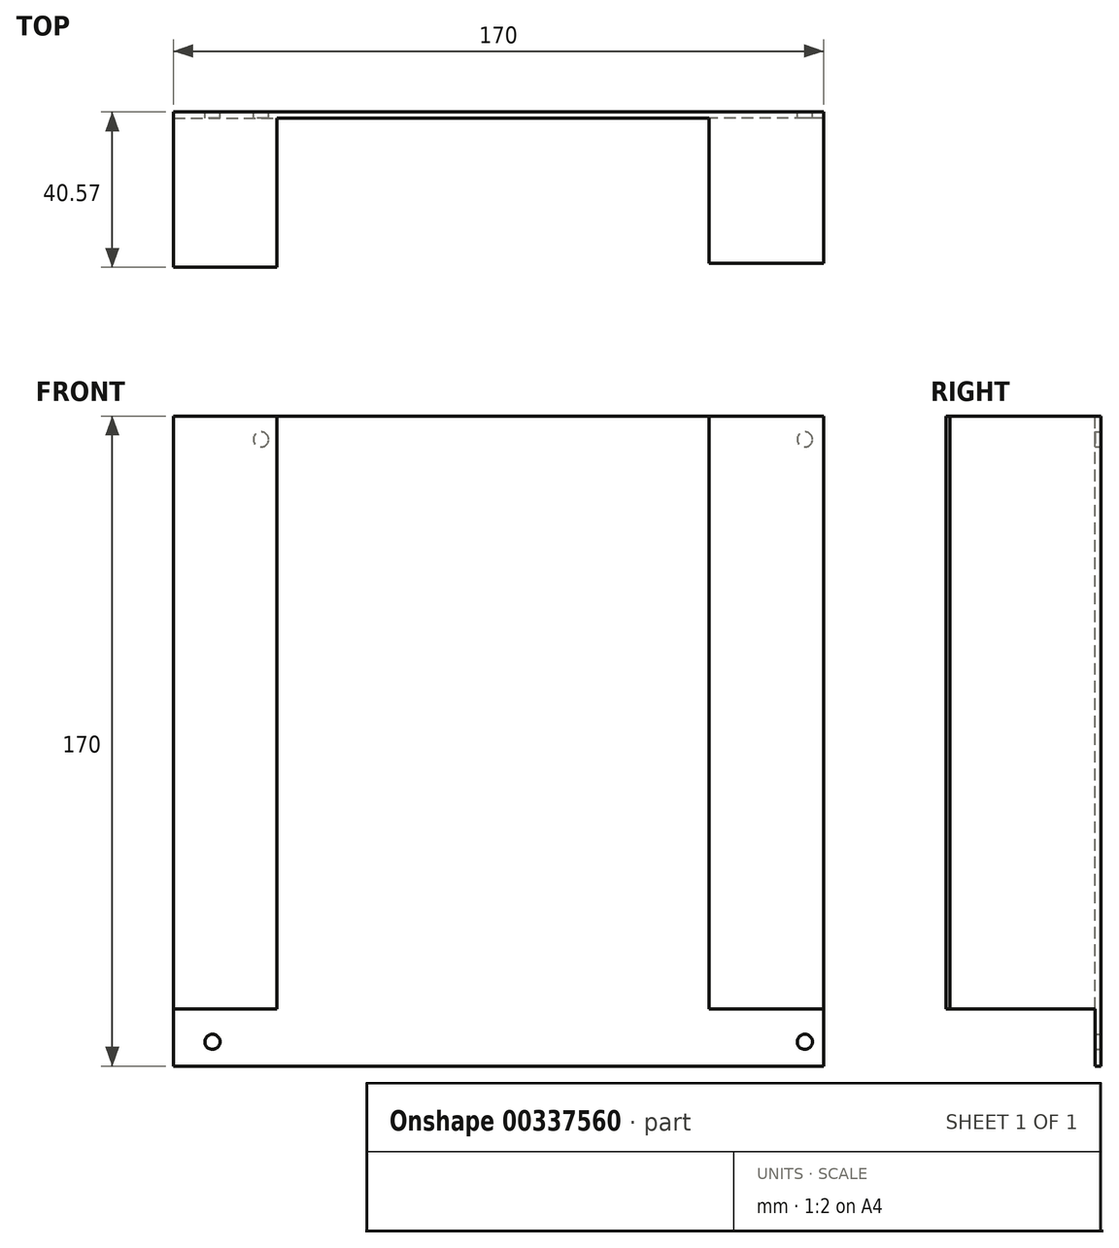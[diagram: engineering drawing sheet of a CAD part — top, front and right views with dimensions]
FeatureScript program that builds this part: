
annotation { "Feature Type Name" : "Feature", "Feature Type Description" : "" }
export const myFeature = defineFeature(function(context is Context, id is Id, definition is map)
    precondition{}
    {
        {
            var Q0;
            Q0=qCreatedBy(makeId("Front.planeOp"),FACE);
            var sketch = newSketch(context, id + "F0", { "sketchPlane" : qUnion([Q0])});
            skLineSegment(sketch, "E0.bottom", {"start": v(0, 0) * mm, "end": v(170, 0) * mm});
            skLineSegment(sketch, "E0.top", {"start": v(0, 170) * mm, "end": v(170, 170) * mm});
            skLineSegment(sketch, "E0.left", {"start": v(0, 0) * mm, "end": v(0, 170) * mm});
            skLineSegment(sketch, "E0.right", {"start": v(170, 0) * mm, "end": v(170, 170) * mm});
            skCircle(sketch, "E1", {"center": v(6.35, 4.88) * mm, "radius": 1.98 * mm});
            skCircle(sketch, "E2", {"center": v(6.35, 159.84) * mm, "radius": 1.98 * mm});
            skCircle(sketch, "E3", {"center": v(163.93, 147.14) * mm, "radius": 1.98 * mm});
            skCircle(sketch, "E4", {"center": v(163.93, 4.88) * mm, "radius": 1.98 * mm});
            skLineSegment(sketch, "E5", {"start": v(6.35, 159.84) * mm, "end": v(6.35, 4.88) * mm, "construction": true});
            skLineSegment(sketch, "E6", {"start": v(163.93, 4.88) * mm, "end": v(6.35, 4.88) * mm, "construction": true});
            skLineSegment(sketch, "E7", {"start": v(163.93, 147.14) * mm, "end": v(163.93, 4.88) * mm, "construction": true});
            skSolve(sketch);
        }
        {
            var Q0;
            Q0 = qSketchRegion(id + "F0", true);
            extrude(context, id + "F1", {"entities" : qUnion([Q0]), "depth" : 1.57 * mm});
        }
        {
            var Q0;
            Q0=makeQuery(id+"F1.opExtrude","CAP_FACE",FACE,{"disambiguationData":[OSD([sQuery(id+"F0.wireOp",EDGE,"E0.bottom"),sQuery(id+"F0.wireOp",EDGE,"E0.top"),sQuery(id+"F0.wireOp",EDGE,"E0.left"),sQuery(id+"F0.wireOp",EDGE,"E0.right"),sQuery(id+"F0.wireOp",EDGE,"E1"),sQuery(id+"F0.wireOp",EDGE,"E2"),sQuery(id+"F0.wireOp",EDGE,"E3"),sQuery(id+"F0.wireOp",EDGE,"E4")])],"isStart":false});
            var sketch = newSketch(context, id + "F2", { "sketchPlane" : qUnion([Q0])});
            skLineSegment(sketch, "E8.bottom", {"start": v(15, 170) * mm, "end": v(170, 170) * mm});
            skLineSegment(sketch, "E8.top", {"start": v(15, 143) * mm, "end": v(170, 143) * mm});
            skLineSegment(sketch, "E8.left", {"start": v(15, 170) * mm, "end": v(15, 143) * mm});
            skLineSegment(sketch, "E8.right", {"start": v(170, 170) * mm, "end": v(170, 143) * mm});
            skSolve(sketch);
        }
        {
            var Q0;
            Q0 = qSketchRegion(id + "F2", true);
            extrude(context, id + "F3", {"entities" : qUnion([Q0]), "operationType" : NewBodyOperationType.ADD, "depth" : 39 * mm});
        }
        {
            var Q0;
            Q0=makeQuery(id+"F1.opExtrude","CAP_FACE",FACE,{"disambiguationData":[OSD([sQuery(id+"F0.wireOp",EDGE,"E0.bottom"),sQuery(id+"F0.wireOp",EDGE,"E0.top"),sQuery(id+"F0.wireOp",EDGE,"E0.left"),sQuery(id+"F0.wireOp",EDGE,"E0.right"),sQuery(id+"F0.wireOp",EDGE,"E1"),sQuery(id+"F0.wireOp",EDGE,"E2"),sQuery(id+"F0.wireOp",EDGE,"E3"),sQuery(id+"F0.wireOp",EDGE,"E4")])],"isStart":false});
            var sketch = newSketch(context, id + "F4", { "sketchPlane" : qUnion([Q0])});
            skLineSegment(sketch, "E9.bottom", {"start": v(15, 0) * mm, "end": v(170, 0) * mm});
            skLineSegment(sketch, "E9.top", {"start": v(15, 30) * mm, "end": v(170, 30) * mm});
            skLineSegment(sketch, "E9.left", {"start": v(15, 0) * mm, "end": v(15, 30) * mm});
            skLineSegment(sketch, "E9.right", {"start": v(170, 0) * mm, "end": v(170, 30) * mm});
            skSolve(sketch);
        }
        {
            var Q0;
            Q0 = qSketchRegion(id + "F4", true);
            extrude(context, id + "F5", {"entities" : qUnion([Q0]), "operationType" : NewBodyOperationType.ADD, "depth" : 38 * mm});
        }
        {
            var Q0;
            Q0=makeQuery(id+"F1.opExtrude","SWEPT_BODY",BODY,{"disambiguationData":[OSD([sQuery(id+"F0.wireOp",EDGE,"E0.bottom"),sQuery(id+"F0.wireOp",EDGE,"E0.top"),sQuery(id+"F0.wireOp",EDGE,"E0.left"),sQuery(id+"F0.wireOp",EDGE,"E0.right"),sQuery(id+"F0.wireOp",EDGE,"E1"),sQuery(id+"F0.wireOp",EDGE,"E2"),sQuery(id+"F0.wireOp",EDGE,"E3"),sQuery(id+"F0.wireOp",EDGE,"E4")])]});
            var Q1;
            Q1=makeQuery(id+"F1.opExtrude","SWEPT_EDGE",EDGE,{"disambiguationData":[OSD([sQuery(id+"F0.wireOp",EDGE,"E0.bottom"),sQuery(id+"F0.wireOp",EDGE,"E0.left")])]});
            transform(context, id + "F6", {"entities" : qUnion([Q0]), "transformType" : TransformType.ROTATION, "transformAxis" : qUnion([Q1]), "angle" : 90 * degree, "oppositeDirection" : true, "makeCopy" : false});
        }
        {
            var Q0;
            Q0=makeQuery(id+"F1.opExtrude","SWEPT_BODY",BODY,{"disambiguationData":[OSD([sQuery(id+"F0.wireOp",EDGE,"E0.bottom"),sQuery(id+"F0.wireOp",EDGE,"E0.top"),sQuery(id+"F0.wireOp",EDGE,"E0.left"),sQuery(id+"F0.wireOp",EDGE,"E0.right"),sQuery(id+"F0.wireOp",EDGE,"E1"),sQuery(id+"F0.wireOp",EDGE,"E2"),sQuery(id+"F0.wireOp",EDGE,"E3"),sQuery(id+"F0.wireOp",EDGE,"E4")])]});
            transform(context, id + "F7", {"entities" : qUnion([Q0]), "transformType" : TransformType.TRANSLATION_3D, "dx" : 170 * mm, "dy" : 0 * mm, "dz" : 0 * mm, "makeCopy" : false});
        }
    });
